# Revit family: 10300800
name_source: partatom
category: Specialty Equipment
units: mm (PartAtom-declared; Revit-internal decimal feet)

## family parameters
Always vertical = Yes
Cut with Voids When Loaded = No
OmniClass Number = 23.40.40.14
OmniClass Title = Food Service Equipment
Part Type = Normal
Room Calculation Point = No
Round Connector Dimension = Use Diameter
Shared = No
Work Plane-Based = No

## types (1)
- Standard
    Default Elevation = 0 mm  [stored 0 ft]
    Description = Serveringsdisk RBP-800
    Height = 1550 mm  [stored 5.0853 ft]
    Length = 802 mm  [stored 2.63123 ft]
    Manufacturer = RUSTFRIE BERGH AS
    Mass = 138 mm  [stored 0.452756 ft]
    Model = 10300800
    URL = https://www.rustfriebergh.no
    Width = 650 mm  [stored 2.13255 ft]

note: [stored X ft] marks values corroborated as IEEE doubles in the binary element streams (Revit-internal decimal feet)

## geometry (parser evidence)
native form markers: Sweep x3
no freeform markers — native parametric forms only
